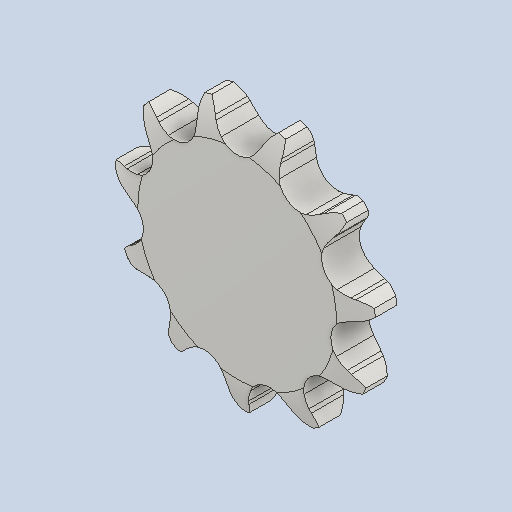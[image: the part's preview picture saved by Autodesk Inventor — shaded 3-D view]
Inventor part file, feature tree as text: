
AUTODESK INVENTOR PART (.ipt)
format: ipt  version: 2022.1 (Build 261234000, 234)  size: 413,184 bytes
history: native  units: mm
features: other x6, extrude x2, pattern_linear x1, pattern_circular x1
ambient origin geometry x8: Origin, YZ Plane, XZ Plane, XY Plane, X Axis, Y Axis, Z Axis, Center Point
bodies: Solid1 (feature_tree)
feature tree (10):
  other  "Perfil de diente teórico"
  other  "Perfil de diente"
  other  "Perfil de sección"
  other  "Cubierta"
  other  "Ramal"
  pattern_linear  "Patrón de ramal"  Spacing1=56.347765mm  [1 undecoded]
  extrude  "Diente teórico"  Depth=5.711987mm
  extrude  "Diente"  Depth=5.1308mm
  pattern_circular  "Patrón de diente"  [2 undecoded]
  other  "Plano síncrono"
note: 3 required parameter values undecoded (feature->parameter linkage not recoverable at this tier; creation-order binding heuristic only, values carry confidence <= 0.55)
